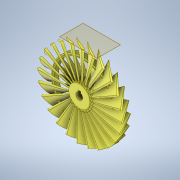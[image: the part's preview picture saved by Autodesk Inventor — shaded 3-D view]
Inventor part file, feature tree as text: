
AUTODESK INVENTOR PART (.ipt)
format: ipt  version: 2021.2 (Build 252289000, 289)  size: 3,472,384 bytes
history: native  units: in
note: dims shown in document units (in); Inventor stores cm internally (conversion verified against a paired STEP export)
features: sketch x5, extrude x4, plane x2, loft x1, revolve x1, pattern_circular x1, other x1
ambient origin geometry x8: Origin, YZ Plane, XZ Plane, XY Plane, X Axis, Y Axis, Z Axis, Center Point
bodies: Solid1 (feature_tree)
feature tree (15):
  extrude  "Extrusion1"  Depth=1.0in
  plane  "Work Plane1"
  plane  "Work Plane2"
  sketch  "Sketch5"  dims[d4=0.6in d15=2.0in]
  sketch  "Sketch6"  dims[d39=0.315in d40=0.125in]
  extrude  "Extrusion5"  Depth=2.0in
  sketch  "Sketch13"  dims[d66=3.9375in d69=0.2in d70=0.0in d75=0.0312in d76=0.0625in d82=0.0625in d83=0.0in d84=90.0deg d85=0.0in d86=90.0deg d90=0.3in d91=0.125in d92=0.5in d93=0.05in d94=0.0in d95=90.0deg d98=0.1681in d99=0.0263in d100=0.5241in d101=0.5596in d102=0.4425in d103=0.0463in d104=0.0247in d106=2.8333in d107=0.047in d108=0.7072in d109=0.7181in d112=0.0546in d113=0.0109in d114=2.2652in d115=0.0806in d116=0.0483in d117=9.4488in d118=360.0deg d120=0.0in d121=0.0in]
  extrude  "Extrusion7"  Depth=0.125in
  loft  "Loft5"
  revolve  "Revolution5"  [1 undecoded]
  pattern_circular  "Circular Pattern7"  [2 undecoded]
  extrude  "Extrusion9"  Depth=0.0625in
  sketch  "Sketch1"  dims[d0=1.0in d1=1.0in d2=0.0777in]
  sketch  "Sketch8"  dims[d41=0.125in d42=0.0in d43=0.0in]
  other  "Edges5"
note: 3 required parameter values undecoded (feature->parameter linkage not recoverable at this tier; creation-order binding heuristic only, values carry confidence <= 0.55)